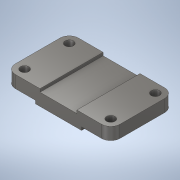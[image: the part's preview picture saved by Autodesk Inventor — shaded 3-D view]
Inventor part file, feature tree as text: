
AUTODESK INVENTOR PART (.ipt)
format: ipt  version: 2020 (Build 240168000, 168)  size: 158,720 bytes
history: native  units: mm
features: extrude x3, sketch x2, fillet x2, mirror x1
ambient origin geometry x8: Origin, YZ Plane, XZ Plane, XY Plane, X Axis, Y Axis, Z Axis, Center Point
bodies: Solid1 (feature_tree)
feature tree (8):
  extrude  "Extrusion1"  Depth=4.0mm
  sketch  "Sketch2"  dims[d2=38.0mm d3=16.0mm d4=44.0mm d5=4.0mm d6=82.0mm d7=0.0mm d8=11.0mm d9=11.0mm d10=12.0mm d11=12.0mm d12=12.0mm d13=12.0mm d14=82.0mm d15=0.0mm d16=82.0mm d17=0.0mm d18=12.0mm d19=12.0mm]
  extrude  "Extrusion2"  Depth=16.0mm
  extrude  "Extrusion3"  Depth=44.0mm
  fillet  "Fillet1"  Radius=4.0mm
  fillet  "Fillet2"  Radius=82.0mm
  mirror  "Mirror1"
  sketch  "Sketch1"  dims[d0=30.0mm d1=4.0mm]
